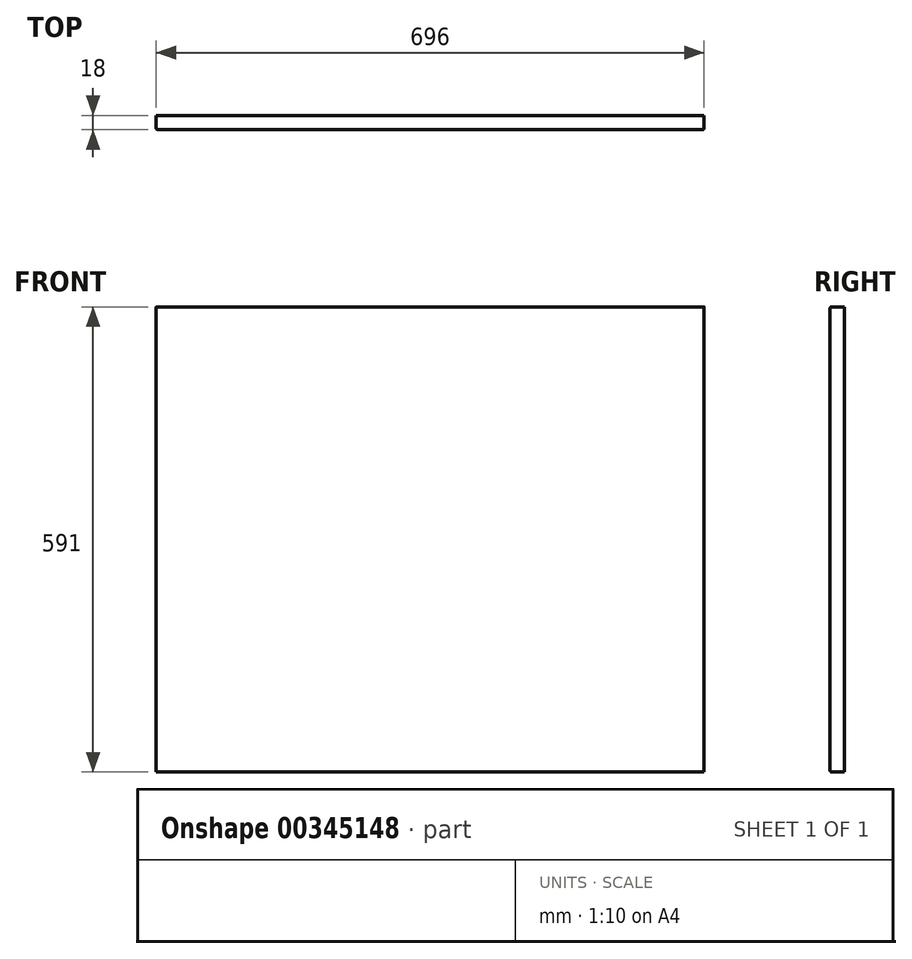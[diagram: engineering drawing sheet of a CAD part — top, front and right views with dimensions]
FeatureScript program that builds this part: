
annotation { "Feature Type Name" : "Feature", "Feature Type Description" : "" }
export const myFeature = defineFeature(function(context is Context, id is Id, definition is map)
    precondition{}
    {
        {
            var Q0;
            Q0=qCreatedBy(makeId("Front.planeOp"),FACE);
            var sketch = newSketch(context, id + "F0", { "sketchPlane" : qUnion([Q0])});
            skLineSegment(sketch, "E0.bottom", {"start": v(0, 0) * mm, "end": v(53.36, 0) * mm});
            skLineSegment(sketch, "E0.top", {"start": v(0, 46.9) * mm, "end": v(53.36, 46.9) * mm});
            skLineSegment(sketch, "E0.left", {"start": v(0, 0) * mm, "end": v(0, 46.9) * mm});
            skLineSegment(sketch, "E0.right", {"start": v(53.36, 0) * mm, "end": v(53.36, 46.9) * mm});
            skSolve(sketch);
        }
        {
            var Q0;
            Q0=makeQuery(id+"F0.imprint","IMPRINT",FACE,{"disambiguationData":[TD([[makeQuery(id+"F0.imprint","IMPRINT",EDGE,{"derivedFrom":sQuery(id+"F0.wireOp",EDGE,"E0.bottom")}),1.0]])]});
            extrude(context, id + "F1", {"entities" : qUnion([Q0]), "depth" : 18 * mm});
        }
        {
            var Q0;
            Q0=makeQuery(id+"F1.opExtrude","SWEPT_FACE",FACE,{"disambiguationData":[OSD([sQuery(id+"F0.wireOp",EDGE,"E0.left")])]});
            extrude(context, id + "F2", {"entities" : qUnion([Q0]), "operationType" : NewBodyOperationType.ADD, "oppositeDirection" : true, "depth" : 696 * mm});
        }
        {
            var Q0;
            {var subQ0=sQuery(id+"F0.wireOp",EDGE,"E0.bottom");Q0=makeQuery(id+"F2.boolean.opBoolean","MERGE",FACE,{"derivedFrom":[makeQuery(id+"F1.opExtrude","SWEPT_FACE",FACE,{"disambiguationData":[OSD([subQ0])]}),makeQuery(id+"F2.opExtrude","SWEPT_FACE",FACE,{"disambiguationData":[OSD([subQ0,sQuery(id+"F0.wireOp",EDGE,"E0.left")])]})]});}
            extrude(context, id + "F3", {"entities" : qUnion([Q0]), "operationType" : NewBodyOperationType.ADD, "oppositeDirection" : true, "depth" : 596 * mm});
        }
        {
            var Q0;
            Q0=makeQuery(id+"F3.opExtrude","CAP_FACE",FACE,{"disambiguationData":[OSD([sQuery(id+"F0.wireOp",EDGE,"E0.bottom"),sQuery(id+"F0.wireOp",EDGE,"E0.left")])],"isStart":false});
            extrude(context, id + "F4", {"entities" : qUnion([Q0]), "operationType" : NewBodyOperationType.REMOVE, "oppositeDirection" : true, "depth" : 5 * mm});
        }
        {
            var Q0;
            {var subQ0=sQuery(id+"F0.wireOp",EDGE,"E0.left");var subQ1=sQuery(id+"F0.wireOp",EDGE,"E0.bottom");Q0=makeQuery(id+"F3.boolean.opBoolean","MERGE",FACE,{"derivedFrom":[makeQuery(id+"F2.boolean.opBoolean","MERGE",FACE,{"derivedFrom":[makeQuery(id+"F1.opExtrude","CAP_FACE",FACE,{"disambiguationData":[OSD([subQ1,sQuery(id+"F0.wireOp",EDGE,"E0.top"),subQ0,sQuery(id+"F0.wireOp",EDGE,"E0.right")])],"isStart":false}),makeQuery(id+"F2.opExtrude","SWEPT_FACE",FACE,{"disambiguationData":[OSD([subQ0]),TDD([makeQuery(id+"F1.opExtrude","CAP_EDGE",EDGE,{"disambiguationData":[OSD([subQ0])],"isStart":false})])]})]}),makeQuery(id+"F3.opExtrude","SWEPT_FACE",FACE,{"disambiguationData":[OSD([subQ1,subQ0]),TDD([makeQuery(id+"F2.boolean.opBoolean","MERGE",EDGE,{"derivedFrom":[makeQuery(id+"F1.opExtrude","CAP_EDGE",EDGE,{"disambiguationData":[OSD([subQ1])],"isStart":false}),makeQuery(id+"F2.opExtrude","SWEPT_EDGE",EDGE,{"disambiguationData":[OSD([subQ1,subQ0]),TDD([makeQuery(id+"F1.opExtrude","CAP_VERTEX",VERTEX,{"disambiguationData":[OSD([subQ1,subQ0])],"isStart":false})])]})]})])]})]});}
            fillet(context, id + "F5", {"entities" : qUnion([Q0]), "radius" : 2 * mm, "tangentPropagation" : true, "allowEdgeOverflow" : false});
        }
    });
